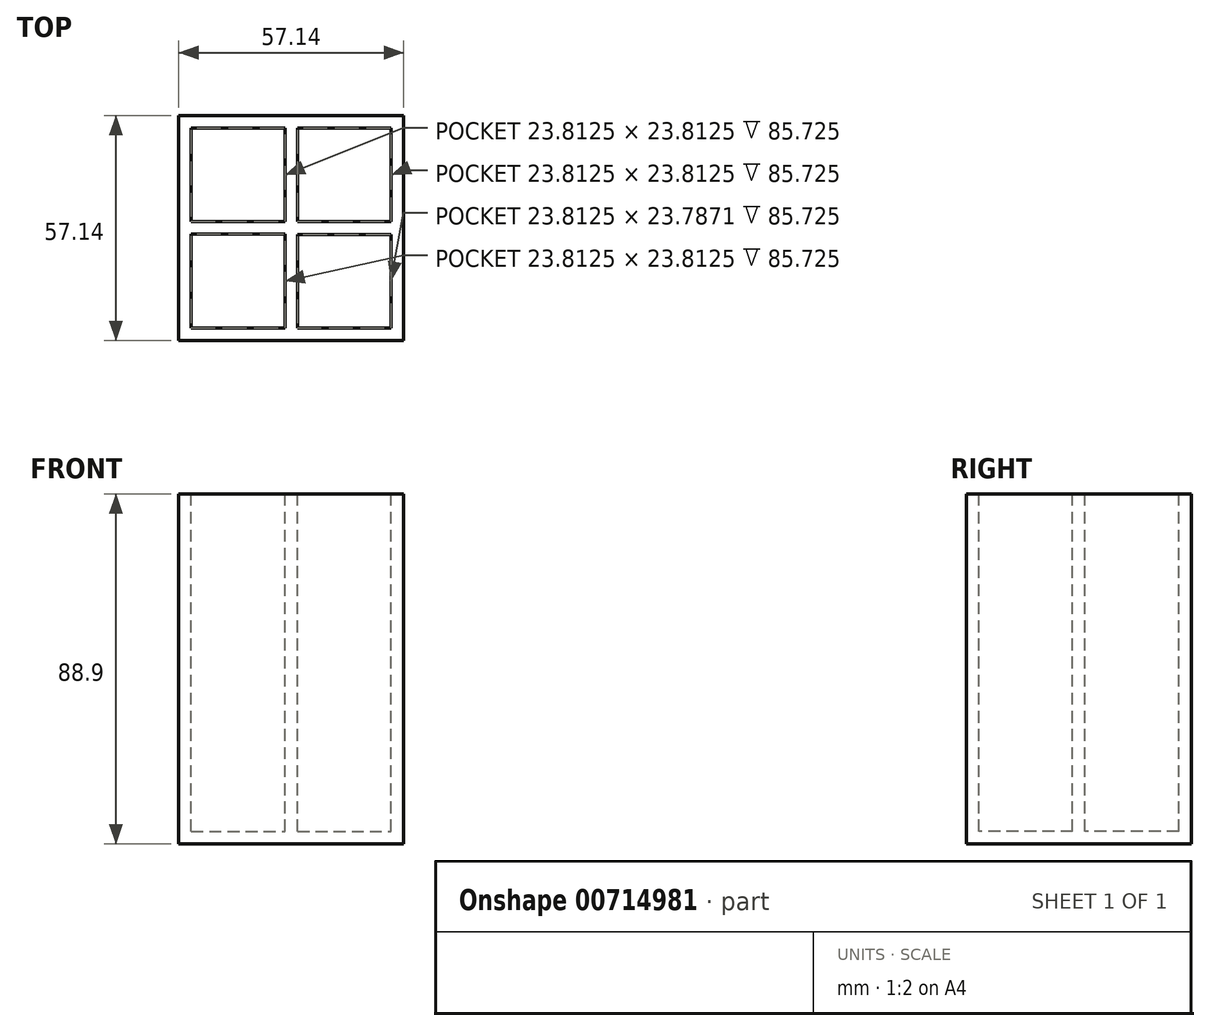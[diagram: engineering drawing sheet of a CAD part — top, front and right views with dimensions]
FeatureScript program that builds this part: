
annotation { "Feature Type Name" : "Feature", "Feature Type Description" : "" }
export const myFeature = defineFeature(function(context is Context, id is Id, definition is map)
    precondition{}
    {
        {
            var Q0;
            Q0=qCreatedBy(makeId("Top.planeOp"),FACE);
            var sketch = newSketch(context, id + "F0", { "sketchPlane" : qUnion([Q0])});
            skLineSegment(sketch, "E0.bottom", {"start": v(28.58, 28.58) * mm, "end": v(-28.58, 28.58) * mm});
            skLineSegment(sketch, "E0.top", {"start": v(28.58, -28.58) * mm, "end": v(-28.57, -28.58) * mm});
            skLineSegment(sketch, "E0.left", {"start": v(28.57, 28.58) * mm, "end": v(28.58, -28.58) * mm});
            skLineSegment(sketch, "E0.right", {"start": v(-28.58, 28.58) * mm, "end": v(-28.57, -28.58) * mm});
            skPoint(sketch, "E0.middle", {"position": v(0, 0) * mm});
            skSolve(sketch);
        }
        {
            var Q0;
            Q0=makeQuery(id+"F0.imprint","IMPRINT",FACE,{"disambiguationData":[TD([[makeQuery(id+"F0.imprint","IMPRINT",EDGE,{"derivedFrom":sQuery(id+"F0.wireOp",EDGE,"E0.bottom")}),1.0]])]});
            extrude(context, id + "F1", {"entities" : qUnion([Q0]), "depth" : 88.9 * mm, "offsetDistance" : 25.4 * mm});
        }
        {
            var Q0;
            Q0=makeQuery(id+"F1.opExtrude","CAP_FACE",FACE,{"disambiguationData":[OSD([sQuery(id+"F0.wireOp",EDGE,"E0.bottom"),sQuery(id+"F0.wireOp",EDGE,"E0.top"),sQuery(id+"F0.wireOp",EDGE,"E0.left"),sQuery(id+"F0.wireOp",EDGE,"E0.right")])],"isStart":false});
            var sketch = newSketch(context, id + "F2", { "sketchPlane" : qUnion([Q0])});
            skLineSegment(sketch, "E1", {"start": v(-28.58, 28.58) * mm, "end": v(-28.58, 25.4) * mm});
            skLineSegment(sketch, "E2", {"start": v(-28.58, 25.4) * mm, "end": v(-25.4, 25.4) * mm});
            skLineSegment(sketch, "E3", {"start": v(-25.4, 25.4) * mm, "end": v(-25.4, -28.58) * mm});
            skLineSegment(sketch, "E4", {"start": v(-25.4, -28.58) * mm, "end": v(-25.4, -25.4) * mm});
            skLineSegment(sketch, "E5", {"start": v(-25.4, -25.4) * mm, "end": v(28.58, -25.4) * mm});
            skLineSegment(sketch, "E6", {"start": v(28.58, -25.4) * mm, "end": v(25.4, -25.4) * mm});
            skLineSegment(sketch, "E7", {"start": v(-25.4, 25.4) * mm, "end": v(28.57, 25.4) * mm});
            skLineSegment(sketch, "E8", {"start": v(25.4, -25.4) * mm, "end": v(25.4, 25.4) * mm});
            skPoint(sketch, "E9", {"position": v(-1.59, 25.4) * mm});
            skPoint(sketch, "E10", {"position": v(1.59, 25.4) * mm});
            skPoint(sketch, "E11", {"position": v(-1.59, -25.4) * mm});
            skPoint(sketch, "E12", {"position": v(1.59, -25.4) * mm});
            skLineSegment(sketch, "E13", {"start": v(-1.59, 25.4) * mm, "end": v(-1.59, -25.4) * mm});
            skLineSegment(sketch, "E14", {"start": v(1.59, 25.4) * mm, "end": v(1.59, -25.4) * mm});
            skPoint(sketch, "E15", {"position": v(-25.4, 1.59) * mm});
            skPoint(sketch, "E16", {"position": v(25.4, 1.59) * mm});
            skPoint(sketch, "E17", {"position": v(25.4, -1.61) * mm});
            skLineSegment(sketch, "E18", {"start": v(-25.4, 1.59) * mm, "end": v(-1.59, 1.59) * mm});
            skLineSegment(sketch, "E19", {"start": v(25.4, 1.59) * mm, "end": v(1.59, 1.59) * mm});
            skLineSegment(sketch, "E20", {"start": v(25.4, -1.61) * mm, "end": v(1.59, -1.61) * mm});
            skLineSegment(sketch, "E21", {"start": v(-25.4, 1.59) * mm, "end": v(-25.4, -1.59) * mm});
            skPoint(sketch, "E22", {"position": v(-25.4, -1.59) * mm});
            skLineSegment(sketch, "E23", {"start": v(-25.4, -1.59) * mm, "end": v(-1.59, -1.59) * mm});
            skSolve(sketch);
        }
        {
            var Q0;
            {var subQ3=sQuery(id+"F2.wireOp",EDGE,"E18");Q0=makeQuery(id+"F2.imprint","IMPRINT",FACE,{"disambiguationData":[TD([[makeQuery(id+"F2.imprint","IMPRINT",EDGE,{"derivedFrom":subQ3}),1.0]])]});}
            var Q1;
            {var subQ5=sQuery(id+"F2.wireOp",EDGE,"E19");Q1=makeQuery(id+"F2.imprint","IMPRINT",FACE,{"disambiguationData":[TD([[makeQuery(id+"F2.imprint","IMPRINT",EDGE,{"derivedFrom":subQ5}),-1.0]])]});}
            var Q2;
            {var subQ5=sQuery(id+"F2.wireOp",EDGE,"E20");Q2=makeQuery(id+"F2.imprint","IMPRINT",FACE,{"disambiguationData":[TD([[makeQuery(id+"F2.imprint","IMPRINT",EDGE,{"derivedFrom":subQ5}),1.0]])]});}
            var Q3;
            {var subQ3=sQuery(id+"F2.wireOp",EDGE,"E23");Q3=makeQuery(id+"F2.imprint","IMPRINT",FACE,{"disambiguationData":[TD([[makeQuery(id+"F2.imprint","IMPRINT",EDGE,{"derivedFrom":subQ3}),-1.0]])]});}
            extrude(context, id + "F3", {"entities" : qUnion([Q0, Q1, Q2, Q3]), "operationType" : NewBodyOperationType.REMOVE, "oppositeDirection" : true, "depth" : 85.72 * mm, "offsetDistance" : 25.4 * mm});
        }
    });
